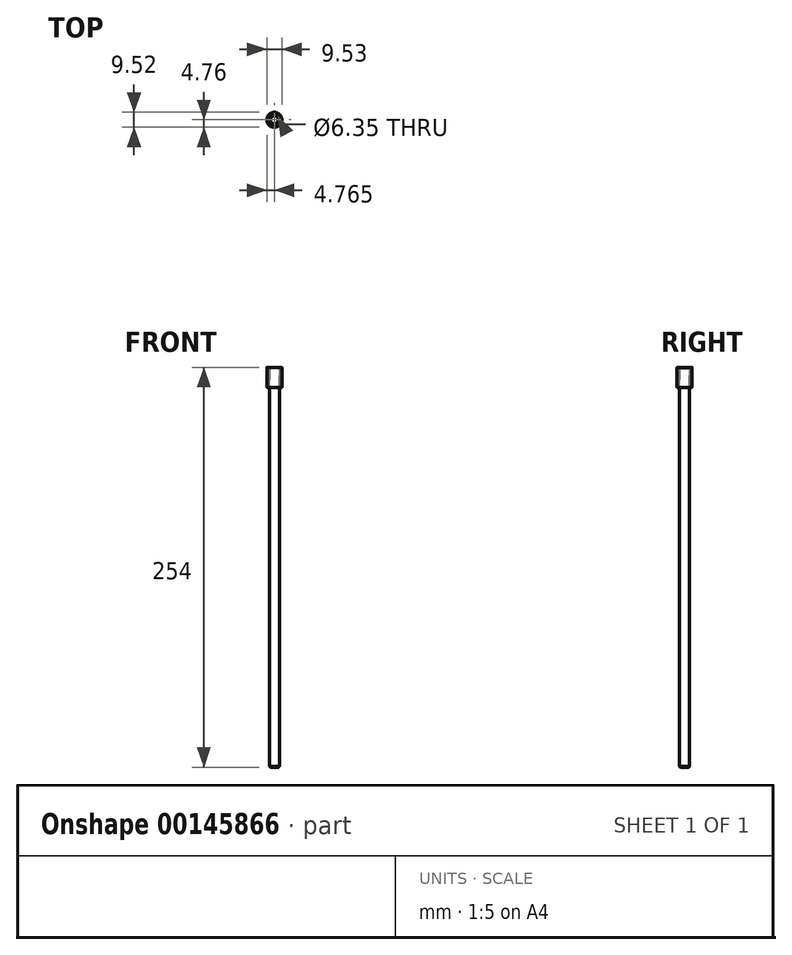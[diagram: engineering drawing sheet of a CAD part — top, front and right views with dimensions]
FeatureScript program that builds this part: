
annotation { "Feature Type Name" : "Feature", "Feature Type Description" : "" }
export const myFeature = defineFeature(function(context is Context, id is Id, definition is map)
    precondition{}
    {
        {
            var Q0;
            Q0=qCreatedBy(makeId("Top.planeOp"),FACE);
            var sketch = newSketch(context, id + "F0", { "sketchPlane" : qUnion([Q0])});
            skCircle(sketch, "E0", {"center": v(0.48, 0) * mm, "radius": 3.18 * mm});
            skCircle(sketch, "E1", {"center": v(0.48, 0) * mm, "radius": 4.76 * mm});
            skSolve(sketch);
        }
        {
            var Q0;
            Q0=qSketchRegion(id+"F0",true);
            extrude(context, id + "F1", {"entities" : qUnion([Q0]), "depth" : 12.7 * mm});
        }
        {
            var Q0;
            Q0=makeQuery(id+"F1.opExtrude","CAP_EDGE",EDGE,{"disambiguationData":[OSD([sQuery(id+"F0.wireOp",EDGE,"E1")])],"isStart":true});
            var Q1;
            Q1=makeQuery(id+"F1.opExtrude","CAP_EDGE",EDGE,{"disambiguationData":[OSD([sQuery(id+"F0.wireOp",EDGE,"E0")])],"isStart":true});
            var Q2;
            Q2=makeQuery(id+"F1.opExtrude","CAP_EDGE",EDGE,{"disambiguationData":[OSD([sQuery(id+"F0.wireOp",EDGE,"E0")])],"isStart":false});
            var Q3;
            Q3=makeQuery(id+"F1.opExtrude","CAP_EDGE",EDGE,{"disambiguationData":[OSD([sQuery(id+"F0.wireOp",EDGE,"E1")])],"isStart":false});
            fillet(context, id + "F2", {"entities" : qUnion([Q0, Q1, Q2, Q3]), "radius" : 0.13 * mm, "tangentPropagation" : true, "allowEdgeOverflow" : false});
        }
        {
            var Q0;
            Q0=makeQuery(id+"F1.opExtrude","CAP_FACE",FACE,{"disambiguationData":[OSD([sQuery(id+"F0.wireOp",EDGE,"E0"),sQuery(id+"F0.wireOp",EDGE,"E1")])],"isStart":false});
            var sketch = newSketch(context, id + "F3", { "sketchPlane" : qUnion([Q0])});
            skCircle(sketch, "E2.0", {"center": v(0.48, 0) * mm, "radius": 3.18 * mm});
            skSolve(sketch);
        }
        {
            var Q0;
            Q0=qSketchRegion(id+"F3",true);
            extrude(context, id + "F4", {"entities" : qUnion([Q0]), "oppositeDirection" : true, "depth" : 254 * mm});
        }
        {
            var Q0;
            Q0=makeQuery(id+"F4.opExtrude","CAP_EDGE",EDGE,{"disambiguationData":[OSD([sQuery(id+"F3.wireOp",EDGE,"E2.0")])],"isStart":false});
            var Q1;
            Q1=makeQuery(id+"F4.opExtrude","CAP_EDGE",EDGE,{"disambiguationData":[OSD([sQuery(id+"F3.wireOp",EDGE,"E2.0")])],"isStart":true});
            chamfer(context, id + "F5", {"entities" : qUnion([Q0, Q1]), "width" : 0.64 * mm, "tangentPropagation" : true});
        }
    });
